# Revit family: Mobile Choral Folio Cabinets
name_source: partatom
category: Generic Models
revit_build: Autodesk Revit Architecture 2012 (Build: 20110916_2132(x64)
units: mm (PartAtom-declared; Revit-internal decimal feet)

## types (3) — shared parameters
2 Columns = Two Columns
2C = 146M022
3 Columns = Three Columns
3C = 146M023
4 Columns = Four Columns
4C = 146M024
Depth = 17.63 "
Description = Mobile Choral Folio Cabinets
Divider Depth = 16.88 "
Divider Laminate = Divider Laminate
Divider Vis 1 = Yes
Height = 50.88 "
Manufacturer = Wenger Corporation
Panel Height = 47.03 "
Shelf Depth = 16.88 "
Shelf Laminate = Shelf Black
URL = http://www.wengercorp.com

## per-type parameters (varying)
| type | Divider Vis 2 | Divider Vis 3 | Part Number | Second Divider Dist | Shelf Array | Shelf Width | Top Width | Width |
| Four Columns | Yes | Yes | 146M024 | 24.13 " | 4 | 11.56 " | 49.25 " | 50.75 " |
| Three Columns | Yes | No | 146M023 | 24.96 " | 3 | 11.98 " | 37.94 " | 39.44 " |
| Two Columns | No | No | 146M022 | 24.96 " | 2 | 11.98 " | 25.25 " | 26.75 " |

note: column(s) folded — value = type name in every type: Model

## geometry (parser evidence)
native form markers: Blend x3, Sweep x9
no freeform markers — native parametric forms only
